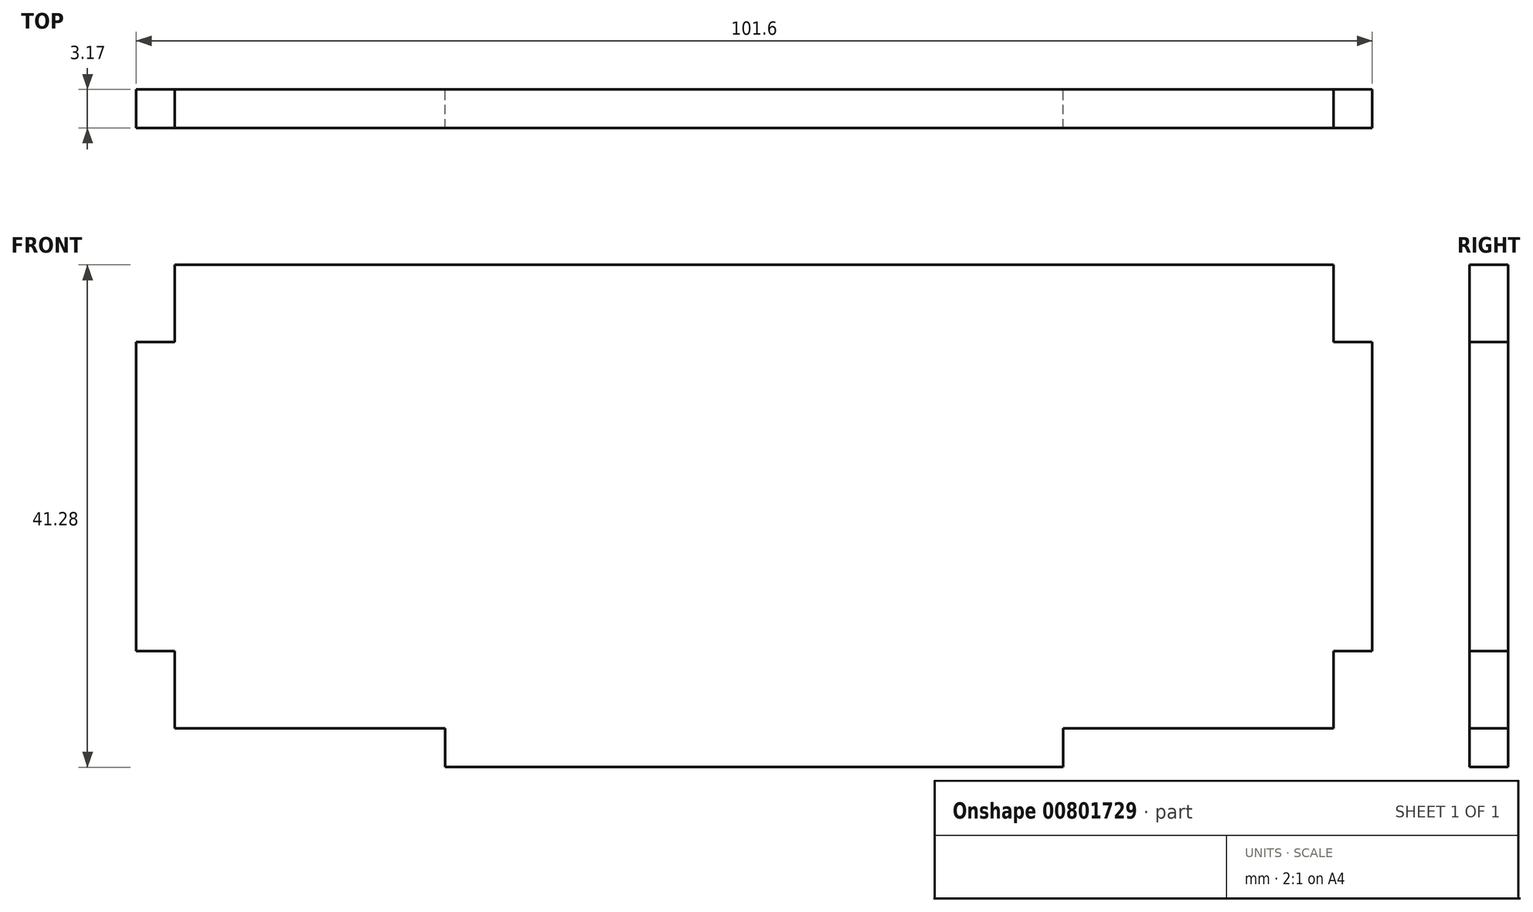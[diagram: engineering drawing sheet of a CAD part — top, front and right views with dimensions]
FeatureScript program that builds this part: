
annotation { "Feature Type Name" : "Feature", "Feature Type Description" : "" }
export const myFeature = defineFeature(function(context is Context, id is Id, definition is map)
    precondition{}
    {
        {
            var Q0;
            Q0=qCreatedBy(makeId("Front.planeOp"),FACE);
            var sketch = newSketch(context, id + "F0", { "sketchPlane" : qUnion([Q0])});
            skLineSegment(sketch, "E0.bottom", {"start": v(47.63, -19.05) * mm, "end": v(25.4, -19.05) * mm});
            skLineSegment(sketch, "E0.top", {"start": v(47.63, 19.05) * mm, "end": v(-47.63, 19.05) * mm});
            skLineSegment(sketch, "E0.left", {"start": v(47.63, -19.05) * mm, "end": v(47.63, -12.7) * mm});
            skLineSegment(sketch, "E0.right", {"start": v(-47.63, -19.05) * mm, "end": v(-47.63, -12.7) * mm});
            skPoint(sketch, "E0.middle", {"position": v(0, 0) * mm});
            skLineSegment(sketch, "E1.top", {"start": v(25.4, -22.23) * mm, "end": v(-25.4, -22.22) * mm});
            skLineSegment(sketch, "E1.left", {"start": v(25.4, -19.05) * mm, "end": v(25.4, -22.23) * mm});
            skLineSegment(sketch, "E1.right", {"start": v(-25.4, -19.05) * mm, "end": v(-25.4, -22.22) * mm});
            skPoint(sketch, "E1.middle", {"position": v(0, -19.05) * mm});
            skLineSegment(sketch, "E2.bottom", {"start": v(50.8, -12.7) * mm, "end": v(47.63, -12.7) * mm});
            skLineSegment(sketch, "E2.top", {"start": v(50.8, 12.7) * mm, "end": v(47.63, 12.7) * mm});
            skLineSegment(sketch, "E2.left", {"start": v(50.8, -12.7) * mm, "end": v(50.8, 12.7) * mm});
            skPoint(sketch, "E2.middle", {"position": v(47.63, 0) * mm});
            skLineSegment(sketch, "E3.bottom", {"start": v(-47.63, -12.7) * mm, "end": v(-50.8, -12.7) * mm});
            skLineSegment(sketch, "E3.top", {"start": v(-47.63, 12.7) * mm, "end": v(-50.8, 12.7) * mm});
            skLineSegment(sketch, "E3.right", {"start": v(-50.8, -12.7) * mm, "end": v(-50.8, 12.7) * mm});
            skPoint(sketch, "E3.middle", {"position": v(-47.63, 0) * mm});
            skLineSegment(sketch, "E4.trimOffspring", {"start": v(-47.63, 12.7) * mm, "end": v(-47.63, 19.05) * mm});
            skPoint(sketch, "E5.orphan", {"position": v(-44.45, 12.7) * mm});
            skPoint(sketch, "E6.orphan", {"position": v(-44.45, -12.7) * mm});
            skLineSegment(sketch, "E7.trimOffspring", {"start": v(-25.4, -19.05) * mm, "end": v(-47.63, -19.05) * mm});
            skPoint(sketch, "E1.bottom.end.orphan", {"position": v(-25.4, -15.87) * mm});
            skPoint(sketch, "E8.orphan", {"position": v(25.4, -15.88) * mm});
            skPoint(sketch, "E9.orphan", {"position": v(44.45, -12.7) * mm});
            skLineSegment(sketch, "E10.trimOffspring", {"start": v(47.63, 12.7) * mm, "end": v(47.63, 19.05) * mm});
            skPoint(sketch, "E11.orphan", {"position": v(44.45, 12.7) * mm});
            skSolve(sketch);
        }
        {
            var Q0;
            Q0 = qSketchRegion(id + "F0", true);
            extrude(context, id + "F1", {"entities" : qUnion([Q0]), "depth" : 3.17 * mm, "offsetDistance" : 25.4 * mm});
        }
    });
